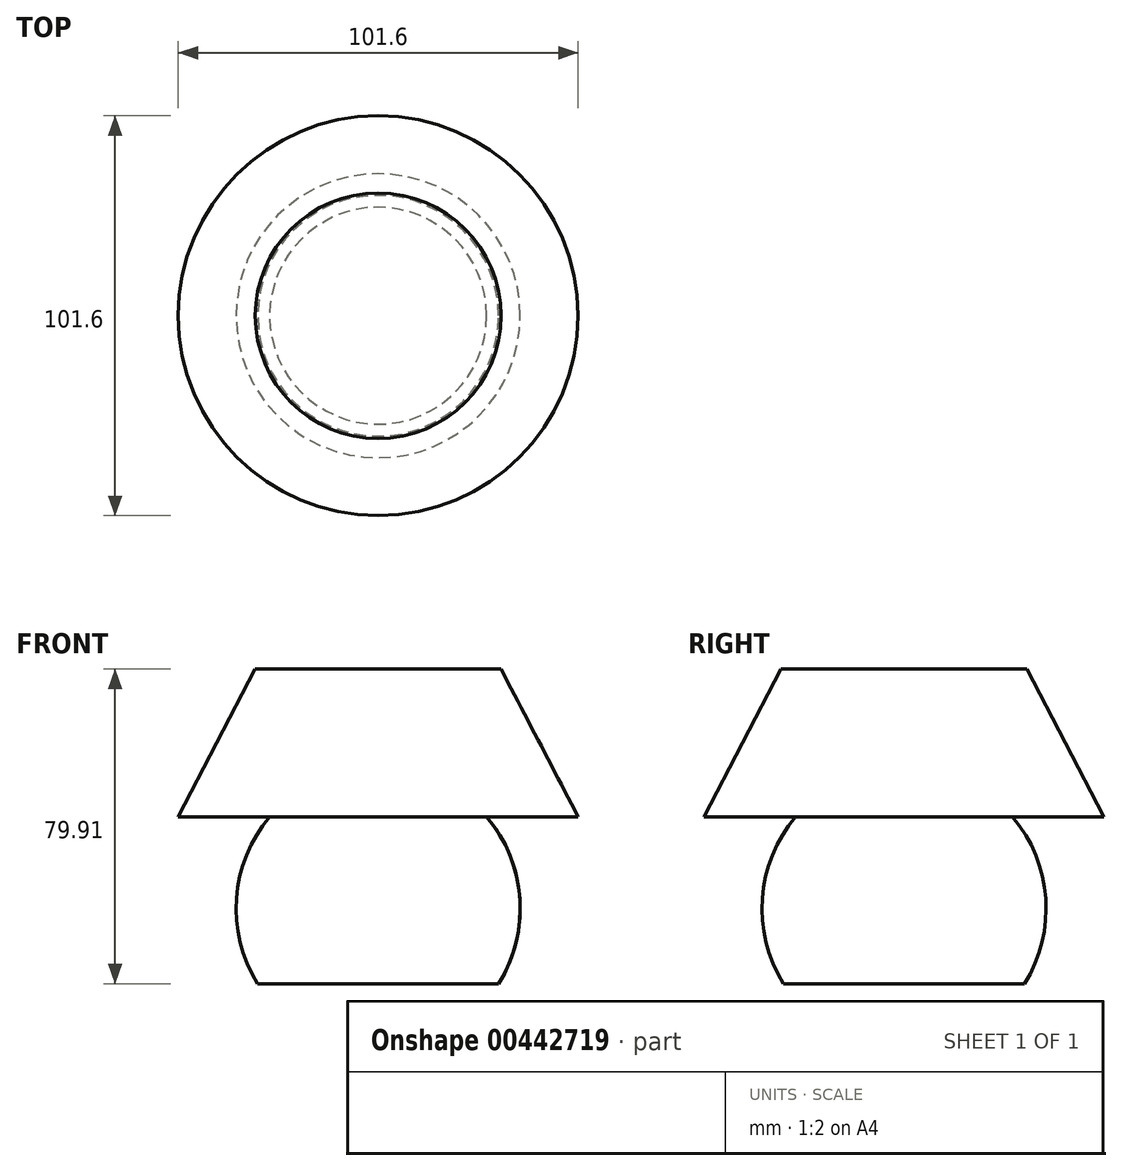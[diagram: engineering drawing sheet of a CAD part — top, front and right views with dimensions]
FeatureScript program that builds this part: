
annotation { "Feature Type Name" : "Feature", "Feature Type Description" : "" }
export const myFeature = defineFeature(function(context is Context, id is Id, definition is map)
    precondition{}
    {
        {
            var Q0;
            Q0=qCreatedBy(makeId("Front.planeOp"),FACE);
            var sketch = newSketch(context, id + "F0", { "sketchPlane" : qUnion([Q0])});
            skLineSegment(sketch, "E0", {"start": v(0, 50.4) * mm, "end": v(-31.21, 50.4) * mm});
            skLineSegment(sketch, "E1", {"start": v(-31.21, 50.4) * mm, "end": v(-50.8, 12.93) * mm});
            skLineSegment(sketch, "E2", {"start": v(-50.8, 12.93) * mm, "end": v(-27.57, 12.93) * mm});
            skArc(sketch, "E3", {"start": v(-27.57, 12.93) * mm, "mid": v(-36, -7.8) * mm, "end": v(-30.6, -29.5) * mm});
            skPoint(sketch, "E4.orphan", {"position": v(0, 12.93) * mm});
            skLineSegment(sketch, "E5", {"start": v(-30.6, -29.5) * mm, "end": v(0, -29.5) * mm});
            skLineSegment(sketch, "E6", {"start": v(0, 50.4) * mm, "end": v(0, -29.5) * mm});
            skSolve(sketch);
        }
        {
            var Q0;
            Q0=makeQuery(id+"F0.imprint","IMPRINT",FACE,{"disambiguationData":[TD([[makeQuery(id+"F0.imprint","IMPRINT",EDGE,{"derivedFrom":sQuery(id+"F0.wireOp",EDGE,"E0")}),1.0]])]});
            var Q1;
            Q1=sQuery(id+"F0.wireOp",EDGE,"E6");
            revolve(context, id + "F1", {"entities" : qUnion([Q0]), "axis" : qUnion([Q1]), "revolveType" : RevolveType.FULL});
        }
    });
